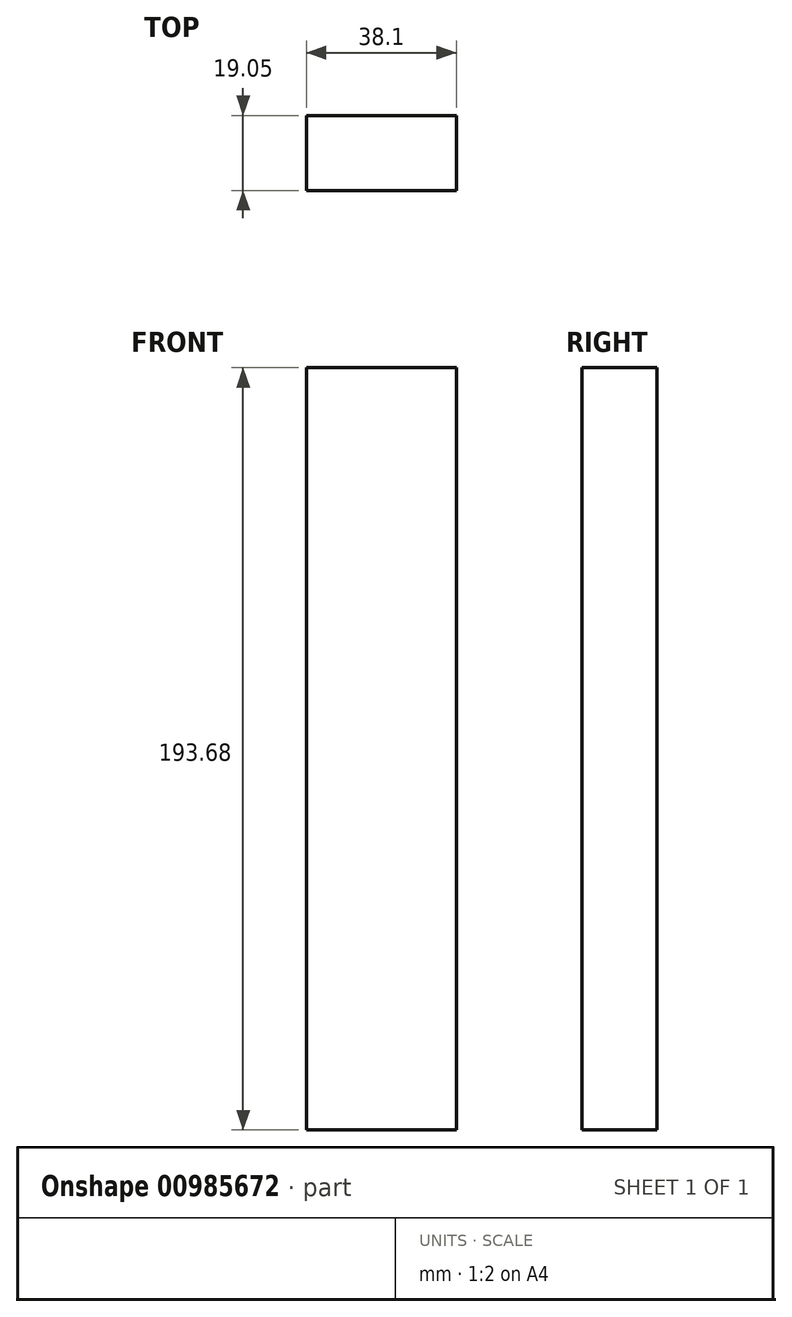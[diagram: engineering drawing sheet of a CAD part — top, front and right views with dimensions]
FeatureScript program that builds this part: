
annotation { "Feature Type Name" : "Feature", "Feature Type Description" : "" }
export const myFeature = defineFeature(function(context is Context, id is Id, definition is map)
    precondition{}
    {
        {
            var Q0;
            Q0=qCreatedBy(makeId("Front.planeOp"),FACE);
            var sketch = newSketch(context, id + "F0", { "sketchPlane" : qUnion([Q0])});
            skLineSegment(sketch, "E0.bottom", {"start": v(19.05, 96.84) * mm, "end": v(-19.05, 96.84) * mm});
            skLineSegment(sketch, "E0.top", {"start": v(19.05, -96.84) * mm, "end": v(-19.05, -96.84) * mm});
            skLineSegment(sketch, "E0.left", {"start": v(19.05, 96.84) * mm, "end": v(19.05, -96.84) * mm});
            skLineSegment(sketch, "E0.right", {"start": v(-19.05, 96.84) * mm, "end": v(-19.05, -96.84) * mm});
            skPoint(sketch, "E0.middle", {"position": v(0, 0) * mm});
            skSolve(sketch);
        }
        {
            var Q0;
            Q0 = qSketchRegion(id + "F0", true);
            extrude(context, id + "F1", {"entities" : qUnion([Q0]), "depth" : 19.05 * mm, "offsetDistance" : 25.4 * mm});
        }
    });
